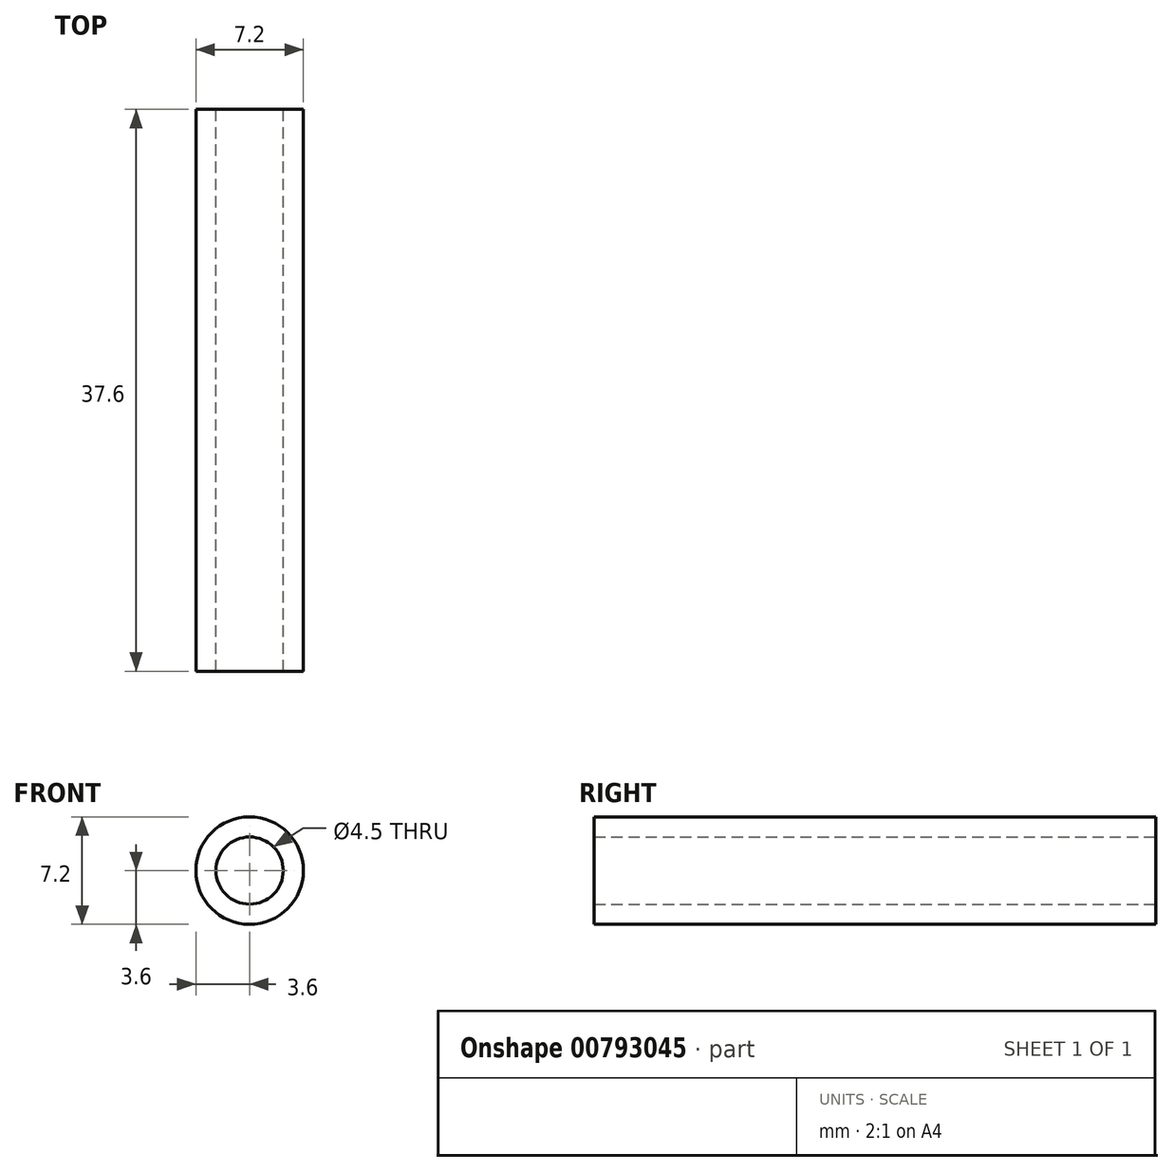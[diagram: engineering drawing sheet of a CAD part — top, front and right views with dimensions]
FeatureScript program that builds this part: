
annotation { "Feature Type Name" : "Feature", "Feature Type Description" : "" }
export const myFeature = defineFeature(function(context is Context, id is Id, definition is map)
    precondition{}
    {
        {
            var Q0;
            Q0=qCreatedBy(makeId("Front.planeOp"),FACE);
            var sketch = newSketch(context, id + "F0", { "sketchPlane" : qUnion([Q0])});
            skCircle(sketch, "E0", {"center": v(0, 0) * mm, "radius": 3.6 * mm});
            skSolve(sketch);
        }
        {
            var Q0;
            Q0 = qSketchRegion(id + "F0", true);
            extrude(context, id + "F1", {"entities" : qUnion([Q0]), "depth" : 37.6 * mm, "offsetDistance" : 25 * mm});
        }
        {
            var Q0;
            Q0=qCreatedBy(makeId("Front.planeOp"),FACE);
            var sketch = newSketch(context, id + "F2", { "sketchPlane" : qUnion([Q0])});
            skCircle(sketch, "E1", {"center": v(0, 0) * mm, "radius": 2.25 * mm});
            skSolve(sketch);
        }
        {
            var Q0;
            Q0 = qSketchRegion(id + "F2", true);
            extrude(context, id + "F3", {"entities" : qUnion([Q0]), "operationType" : NewBodyOperationType.REMOVE, "depth" : 38.1 * mm, "offsetDistance" : 25 * mm});
        }
        {
            var Q0;
            Q0=qCreatedBy(makeId("Right.planeOp"),FACE);
            var sketch = newSketch(context, id + "F4", { "sketchPlane" : qUnion([Q0])});
            skLineSegment(sketch, "E2", {"start": v(-7.97, 3.62) * mm, "end": v(-7.97, 5.5) * mm});
            skLineSegment(sketch, "E3", {"start": v(-7.97, 5.5) * mm, "end": v(-9.97, 5.5) * mm});
            skLineSegment(sketch, "E4", {"start": v(-9.97, 5.5) * mm, "end": v(-9.97, 3.6) * mm});
            skSolve(sketch);
        }
        {
            var Q0;
            Q0=sQuery(id+"F4.wireOp",EDGE,"E3");
            var Q1;
            Q1=sQuery(id+"F4.wireOp",EDGE,"E4");
            var Q2;
            Q2=sQuery(id+"F4.wireOp",EDGE,"E2");
            var Q3;
            Q3=makeQuery(id+"F1.opExtrude","SWEPT_FACE",FACE,{"disambiguationData":[OSD([sQuery(id+"F0.wireOp",EDGE,"E0")])]});
            revolve(context, id + "F5", {"bodyType" : ToolBodyType.SURFACE, "operationType" : NewBodyOperationType.ADD, "surfaceOperationType" : NewSurfaceOperationType.NEW, "surfaceEntities" : qUnion([Q0, Q1, Q2]), "axis" : qUnion([Q3]), "revolveType" : RevolveType.FULL});
        }
        {
            var Q0;
            Q0=qCreatedBy(makeId("Right.planeOp"),FACE);
            var sketch = newSketch(context, id + "F6", { "sketchPlane" : qUnion([Q0])});
            skLineSegment(sketch, "E5", {"start": v(-17.04, 3.6) * mm, "end": v(-17.04, 6.32) * mm});
            skLineSegment(sketch, "E6", {"start": v(-17.04, 6.32) * mm, "end": v(-19.04, 6.32) * mm});
            skLineSegment(sketch, "E7", {"start": v(-19.04, 6.32) * mm, "end": v(-19.04, 3.6) * mm});
            skSolve(sketch);
        }
        {
            var Q0;
            Q0=sQuery(id+"F6.wireOp",EDGE,"E6");
            var Q1;
            Q1=sQuery(id+"F6.wireOp",EDGE,"E7");
            var Q2;
            Q2=sQuery(id+"F6.wireOp",EDGE,"E5");
            var Q3;
            Q3=makeQuery(id+"F1.opExtrude","SWEPT_FACE",FACE,{"disambiguationData":[OSD([sQuery(id+"F0.wireOp",EDGE,"E0")])]});
            revolve(context, id + "F7", {"bodyType" : ToolBodyType.SURFACE, "surfaceOperationType" : NewSurfaceOperationType.NEW, "surfaceEntities" : qUnion([Q0, Q1, Q2]), "axis" : qUnion([Q3]), "revolveType" : RevolveType.FULL});
        }
        {
            var Q0;
            Q0=makeQuery(id+"F7.opRevolve","SWEPT_EDGE",EDGE,{"disambiguationData":[OSD([sQuery(id+"F6.wireOp",VERTEX,"E7.start")])]});
            fillet(context, id + "F8", {"entities" : qUnion([Q0]), "radius" : 0.5 * mm, "tangentPropagation" : true, "allowEdgeOverflow" : false});
        }
        {
            var Q0;
            Q0=makeQuery(id+"F7.opRevolve","SWEPT_EDGE",EDGE,{"disambiguationData":[OSD([sQuery(id+"F6.wireOp",VERTEX,"E5.end")])]});
            fillet(context, id + "F9", {"entities" : qUnion([Q0]), "radius" : 0.5 * mm, "tangentPropagation" : true, "allowEdgeOverflow" : false});
        }
    });
